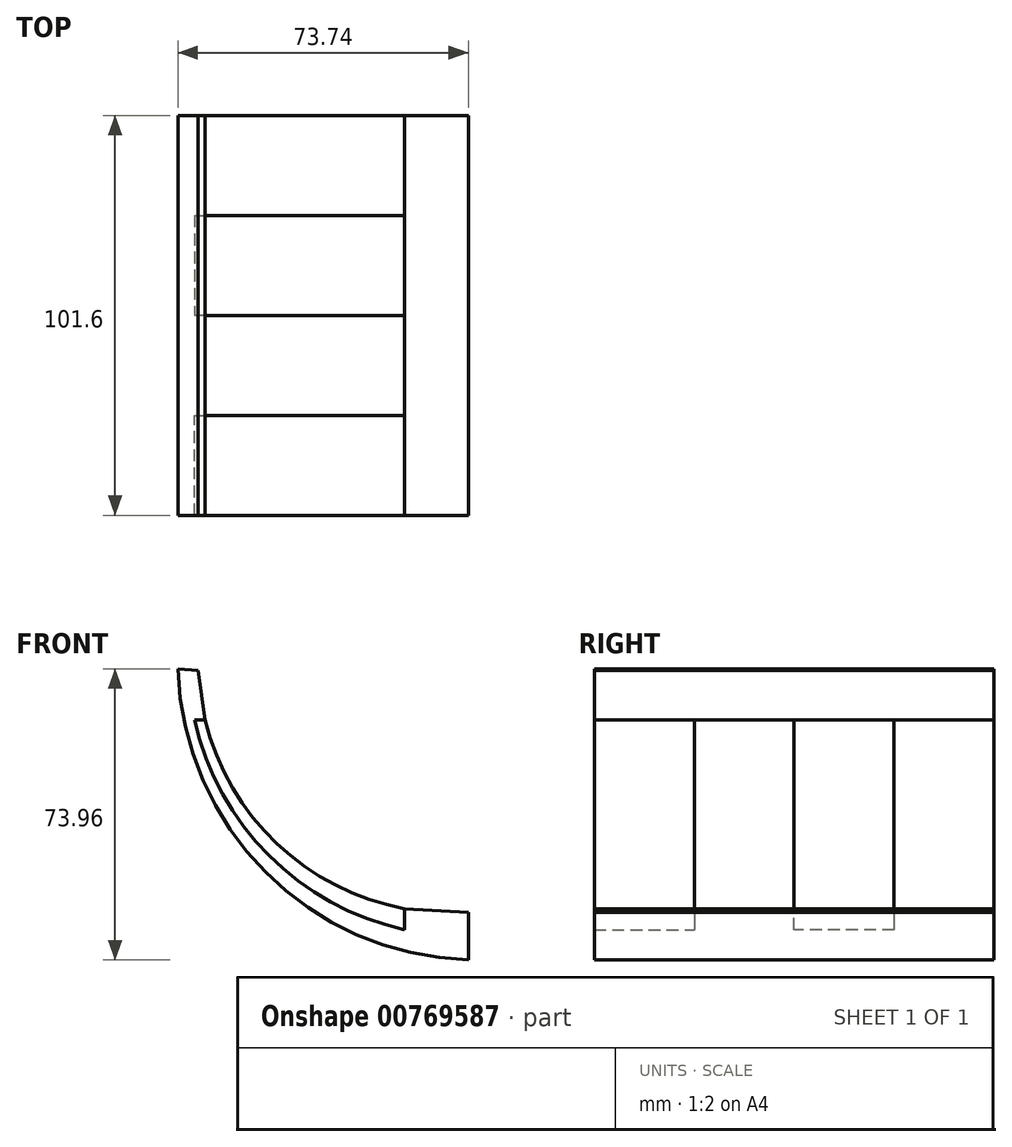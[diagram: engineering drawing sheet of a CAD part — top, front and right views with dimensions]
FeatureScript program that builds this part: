
annotation { "Feature Type Name" : "Feature", "Feature Type Description" : "" }
export const myFeature = defineFeature(function(context is Context, id is Id, definition is map)
    precondition{}
    {
        {
            var Q0;
            Q0=qCreatedBy(makeId("Front.planeOp"),FACE);
            var sketch = newSketch(context, id + "F0", { "sketchPlane" : qUnion([Q0])});
            skArc(sketch, "E0", {"start": v(0, 73.96) * mm, "mid": v(22.24, 22.4) * mm, "end": v(73.74, 0) * mm});
            skArc(sketch, "E1", {"start": v(5.06, 73.52) * mm, "mid": v(26.46, 28.33) * mm, "end": v(73.74, 12.1) * mm});
            skLineSegment(sketch, "E2", {"start": v(0, 73.96) * mm, "end": v(5.06, 73.52) * mm});
            skLineSegment(sketch, "E3", {"start": v(73.74, 12.1) * mm, "end": v(73.74, 0) * mm});
            skSolve(sketch);
        }
        {
            var Q0;
            Q0 = qSketchRegion(id + "F0", true);
            extrude(context, id + "F1", {"entities" : qUnion([Q0]), "depth" : 76.2 * mm, "offsetDistance" : 25.4 * mm});
        }
        {
            var Q0;
            Q0 = qSketchRegion(id + "F0", true);
            extrude(context, id + "F2", {"entities" : qUnion([Q0]), "operationType" : NewBodyOperationType.REMOVE, "oppositeDirection" : true, "depth" : -50.8 * mm, "offsetDistance" : 25.4 * mm});
        }
        {
            var Q0;
            Q0=makeQuery(id+"F2.boolean.opBoolean","COPY",FACE,{"derivedFrom":makeQuery(id+"F2.opExtrude","CAP_FACE",FACE,{"disambiguationData":[OSD([sQuery(id+"F0.wireOp",EDGE,"E0"),sQuery(id+"F0.wireOp",EDGE,"E1"),sQuery(id+"F0.wireOp",EDGE,"E2"),sQuery(id+"F0.wireOp",EDGE,"E3")])],"isStart":false})});
            var sketch = newSketch(context, id + "F3", { "sketchPlane" : qUnion([Q0])});
            skArc(sketch, "E4", {"start": v(-73.74, 6.05) * mm, "mid": v(-24.33, 25.37) * mm, "end": v(-2.53, 73.74) * mm});
            skArc(sketch, "E5", {"start": v(-73.74, 0) * mm, "mid": v(-22.2, 22.36) * mm, "end": v(0, 73.96) * mm});
            skLineSegment(sketch, "E6", {"start": v(-2.53, 73.74) * mm, "end": v(0, 73.96) * mm});
            skLineSegment(sketch, "E7", {"start": v(-73.74, 6.05) * mm, "end": v(-73.74, 0) * mm});
            skLineSegment(sketch, "E8", {"start": v(-2.53, 73.74) * mm, "end": v(-5.06, 73.52) * mm});
            skLineSegment(sketch, "E9", {"start": v(-5.06, 73.52) * mm, "end": v(-6.86, 60.94) * mm});
            skLineSegment(sketch, "E10", {"start": v(-6.86, 60.94) * mm, "end": v(-4.18, 60.94) * mm});
            skLineSegment(sketch, "E11", {"start": v(-73.74, 6.05) * mm, "end": v(-73.74, 12.1) * mm});
            skLineSegment(sketch, "E12", {"start": v(-57.52, 7.7) * mm, "end": v(-57.52, 13.04) * mm});
            skLineSegment(sketch, "E13", {"start": v(-57.52, 13.04) * mm, "end": v(-73.74, 12.1) * mm});
            skSolve(sketch);
        }
        {
            var Q0;
            Q0 = qSketchRegion(id + "F3", true);
            extrude(context, id + "F4", {"entities" : qUnion([Q0]), "operationType" : NewBodyOperationType.ADD, "depth" : 50.8 * mm, "offsetDistance" : 25.4 * mm});
        }
        {
            var Q0;
            Q0 = qSketchRegion(id + "F0", true);
            extrude(context, id + "F5", {"entities" : qUnion([Q0]), "operationType" : NewBodyOperationType.ADD, "depth" : 25.4 * mm, "offsetDistance" : 25.4 * mm});
        }
        {
            var Q0;
            Q0 = qSketchRegion(id + "F3", true);
            extrude(context, id + "F6", {"entities" : qUnion([Q0]), "operationType" : NewBodyOperationType.ADD, "depth" : -50.8 * mm, "offsetDistance" : 25.4 * mm});
        }
    });
